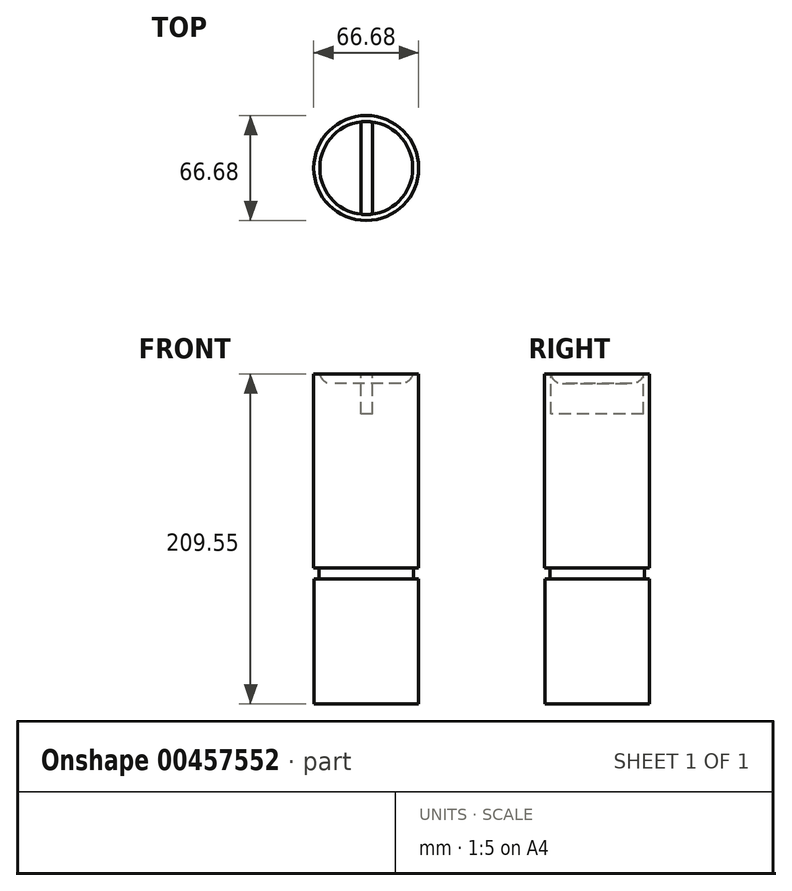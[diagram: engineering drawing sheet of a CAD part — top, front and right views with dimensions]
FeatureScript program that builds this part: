
annotation { "Feature Type Name" : "Feature", "Feature Type Description" : "" }
export const myFeature = defineFeature(function(context is Context, id is Id, definition is map)
    precondition{}
    {
        {
            var Q0;
            Q0=qCreatedBy(makeId("Top.planeOp"),FACE);
            var sketch = newSketch(context, id + "F0", { "sketchPlane" : qUnion([Q0])});
            skCircle(sketch, "E0", {"center": v(-20.5, 21.84) * mm, "radius": 33.12 * mm});
            skSolve(sketch);
        }
        {
            var Q0;
            Q0=makeQuery(id+"F0.imprint","IMPRINT",FACE,{"disambiguationData":[TD([[makeQuery(id+"F0.imprint","IMPRINT",EDGE,{"derivedFrom":sQuery(id+"F0.wireOp",EDGE,"E0")}),1.0]])]});
            extrude(context, id + "F1", {"entities" : qUnion([Q0]), "depth" : 79.5 * mm});
        }
        {
            var Q0;
            Q0=makeQuery(id+"F1.opExtrude","CAP_FACE",FACE,{"disambiguationData":[OSD([sQuery(id+"F0.wireOp",EDGE,"E0")])],"isStart":false});
            var sketch = newSketch(context, id + "F2", { "sketchPlane" : qUnion([Q0])});
            skCircle(sketch, "E1", {"center": v(-20.5, 21.84) * mm, "radius": 29.95 * mm});
            skSolve(sketch);
        }
        {
            var Q0;
            Q0=makeQuery(id+"F2.imprint","IMPRINT",FACE,{"disambiguationData":[TD([[makeQuery(id+"F2.imprint","IMPRINT",EDGE,{"derivedFrom":sQuery(id+"F2.wireOp",EDGE,"E1")}),1.0]])]});
            extrude(context, id + "F3", {"entities" : qUnion([Q0]), "operationType" : NewBodyOperationType.ADD, "depth" : 6.86 * mm});
        }
        {
            var Q0;
            Q0=makeQuery(id+"F3.opExtrude","CAP_FACE",FACE,{"disambiguationData":[OSD([sQuery(id+"F2.wireOp",EDGE,"E1")])],"isStart":false});
            var sketch = newSketch(context, id + "F4", { "sketchPlane" : qUnion([Q0])});
            skCircle(sketch, "E2", {"center": v(-20.5, 21.84) * mm, "radius": 33.34 * mm});
            skSolve(sketch);
        }
        {
            var Q0;
            Q0=makeQuery(id+"F4.imprint","IMPRINT",FACE,{"disambiguationData":[TD([[makeQuery(id+"F4.imprint","IMPRINT",EDGE,{"derivedFrom":makeQuery(id+"F3.opExtrude","CAP_EDGE",EDGE,{"disambiguationData":[OSD([sQuery(id+"F2.wireOp",EDGE,"E1")])],"isStart":false})}),1.0]])]});
            var Q1;
            Q1=makeQuery(id+"F4.imprint","IMPRINT",FACE,{"disambiguationData":[TD([[makeQuery(id+"F4.imprint","IMPRINT",EDGE,{"derivedFrom":sQuery(id+"F4.wireOp",EDGE,"E2")}),1.0]])]});
            extrude(context, id + "F5", {"entities" : qUnion([Q0, Q1]), "operationType" : NewBodyOperationType.ADD, "depth" : 123.19 * mm});
        }
        {
            var Q0;
            Q0=makeQuery(id+"F5.opExtrude","CAP_FACE",FACE,{"disambiguationData":[OSD([sQuery(id+"F4.wireOp",EDGE,"E2")])],"isStart":false});
            var sketch = newSketch(context, id + "F6", { "sketchPlane" : qUnion([Q0])});
            skCircle(sketch, "E3", {"center": v(-20.5, 21.84) * mm, "radius": 29.5 * mm});
            skSolve(sketch);
        }
        {
            var Q0;
            Q0=makeQuery(id+"F6.imprint","IMPRINT",FACE,{"disambiguationData":[TD([[makeQuery(id+"F6.imprint","IMPRINT",EDGE,{"derivedFrom":sQuery(id+"F6.wireOp",EDGE,"E3")}),1.0]])]});
            extrude(context, id + "F7", {"entities" : qUnion([Q0]), "operationType" : NewBodyOperationType.REMOVE, "oppositeDirection" : true, "depth" : 6.1 * mm});
        }
        {
            var Q0;
            Q0=makeQuery(id+"F7.boolean.opBoolean","COPY",EDGE,{"derivedFrom":makeQuery(id+"F7.opExtrude","CAP_EDGE",EDGE,{"disambiguationData":[OSD([sQuery(id+"F6.wireOp",EDGE,"E3")])],"isStart":false})});
            fillet(context, id + "F8", {"entities" : qUnion([Q0]), "radius" : 7.62 * mm, "tangentPropagation" : true, "allowEdgeOverflow" : false});
        }
        {
            var Q0;
            Q0=makeQuery(id+"F5.opExtrude","CAP_FACE",FACE,{"disambiguationData":[OSD([sQuery(id+"F4.wireOp",EDGE,"E2")])],"isStart":false});
            var sketch = newSketch(context, id + "F9", { "sketchPlane" : qUnion([Q0])});
            skLineSegment(sketch, "E4.bottom", {"start": v(-23.85, 52.85) * mm, "end": v(-16.64, 52.85) * mm});
            skLineSegment(sketch, "E4.top", {"start": v(-23.85, -8.8) * mm, "end": v(-16.64, -8.8) * mm});
            skLineSegment(sketch, "E4.left", {"start": v(-23.85, 52.85) * mm, "end": v(-23.85, -8.8) * mm});
            skLineSegment(sketch, "E4.right", {"start": v(-16.64, 52.85) * mm, "end": v(-16.64, -8.8) * mm});
            skSolve(sketch);
        }
        {
            var Q0;
            {var subQ0=sQuery(id+"F9.wireOp",EDGE,"E4.left");var subQ1=makeQuery(id+"F8.opFillet","BLEND_EDGE",EDGE,{"blendedFrom":[makeQuery(id+"F7.boolean.opBoolean","COPY",EDGE,{"derivedFrom":makeQuery(id+"F7.opExtrude","CAP_EDGE",EDGE,{"disambiguationData":[OSD([sQuery(id+"F6.wireOp",EDGE,"E3")])],"isStart":false})}),makeQuery(id+"F5.opExtrude","CAP_FACE",FACE,{"disambiguationData":[OSD([sQuery(id+"F4.wireOp",EDGE,"E2")])],"isStart":false})],"blendedInto":[makeQuery(id+"F5.opExtrude","CAP_FACE",FACE,{"disambiguationData":[OSD([sQuery(id+"F4.wireOp",EDGE,"E2")])],"isStart":false})]});var subQ2=makeQuery(id+"F9.imprint","INTERSECT",VERTEX,{"disambiguationData":[OD(0.0)],"derivedFrom":[subQ1,subQ0]});Q0=makeQuery(id+"F9.imprint","IMPRINT",FACE,{"disambiguationData":[TD([[makeQuery(id+"F9.imprint","IMPRINT",EDGE,{"disambiguationData":[TD([[subQ2,-1.0]])],"derivedFrom":subQ0}),1.0]])]});}
            extrude(context, id + "F10", {"entities" : qUnion([Q0]), "oppositeDirection" : true, "depth" : 25.4 * mm});
        }
    });
